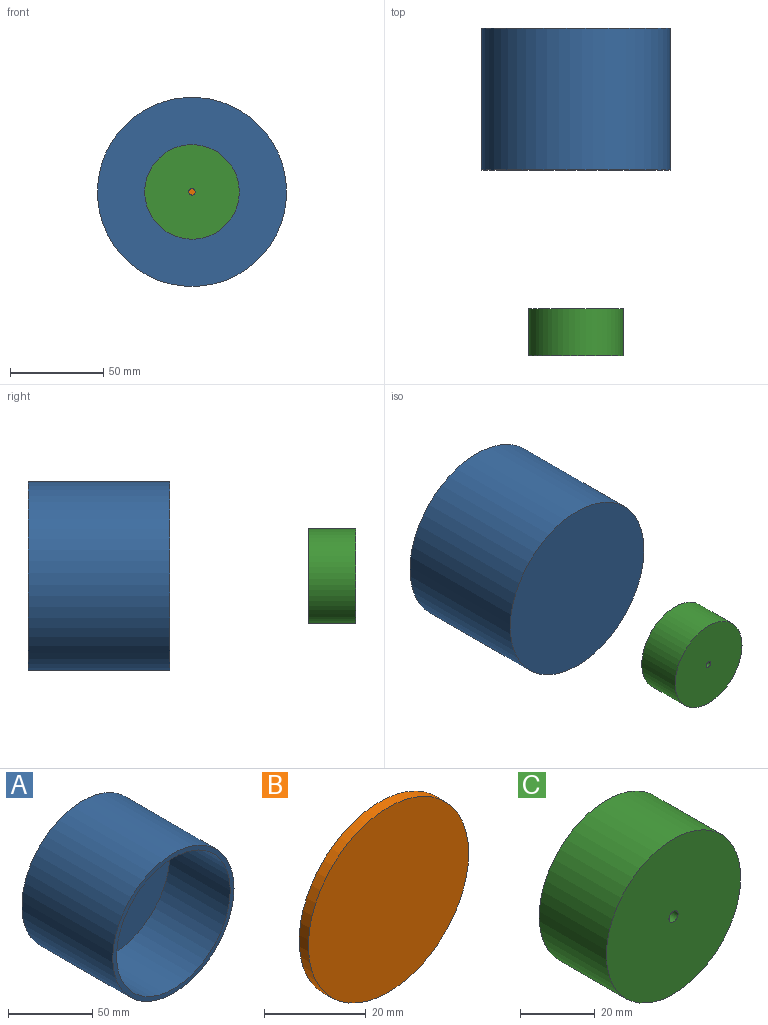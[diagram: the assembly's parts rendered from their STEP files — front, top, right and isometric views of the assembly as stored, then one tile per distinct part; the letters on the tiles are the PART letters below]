
ASSEMBLY  parts=3 mates=2
PART A: 5 faces, bbox 101.6x76.2x101.6 mm
  f0: cylinder r=47.62mm len=95.25mm, axis (0,1,0), area 15201.2mm2, adj f2,f4
  f1: cylinder r=50.8mm len=101.6mm, axis (0,1,0), area 24322mm2, adj f2,f3
  f2: plane 101.6x101.6mm, normal (0,-1,0), area 981.7mm2, adj f0,f1
  f3: plane 101.6x101.6mm, normal (0,1,0), area 8107.3mm2, adj f1
  f4: plane 95.25x95.25mm, normal (0,-1,0), area 7125.6mm2, adj f0
PART B: 3 faces, bbox 44.5x2.5x44.5 mm
  f0: cylinder r=22.23mm len=44.45mm, axis (0,1,0), area 354.7mm2, adj f1,f2
  f1: plane 44.45x44.45mm, normal (0,-1,0), area 1551.8mm2, adj f0
  f2: plane 44.45x44.45mm, normal (0,1,0), area 1551.8mm2, adj f0
PART C: 4 faces, bbox 50.8x25.4x50.8 mm
  f0: cylinder r=1.71mm len=25.4mm, axis (0,1,0), area 273.6mm2, adj f2,f3
  f1: cylinder r=25.4mm len=50.8mm, axis (0,1,0), area 4053.7mm2, adj f2,f3
  f2: plane 50.8x50.8mm, normal (0,-1,0), area 2017.6mm2, adj f0,f1
  f3: plane 50.8x50.8mm, normal (0,1,0), area 2017.6mm2, adj f0,f1
PLACE A rot(axis=(0.71,0,-0.71),180deg) t=(-43.57,-85.86,-40.8)mm fixed
PLACE B t=(-43.57,-160.33,-40.8)mm
PLACE C t=(-43.57,-160.33,-40.8)mm
MATE slider C.f0 <-> A.f0  axis (0,1,0) through (-43.57,-185.73,-40.8)mm
MATE fastened C.f0 <-> B.f0  axis (0,1,0) through (-43.57,-160.33,-40.8)mm
